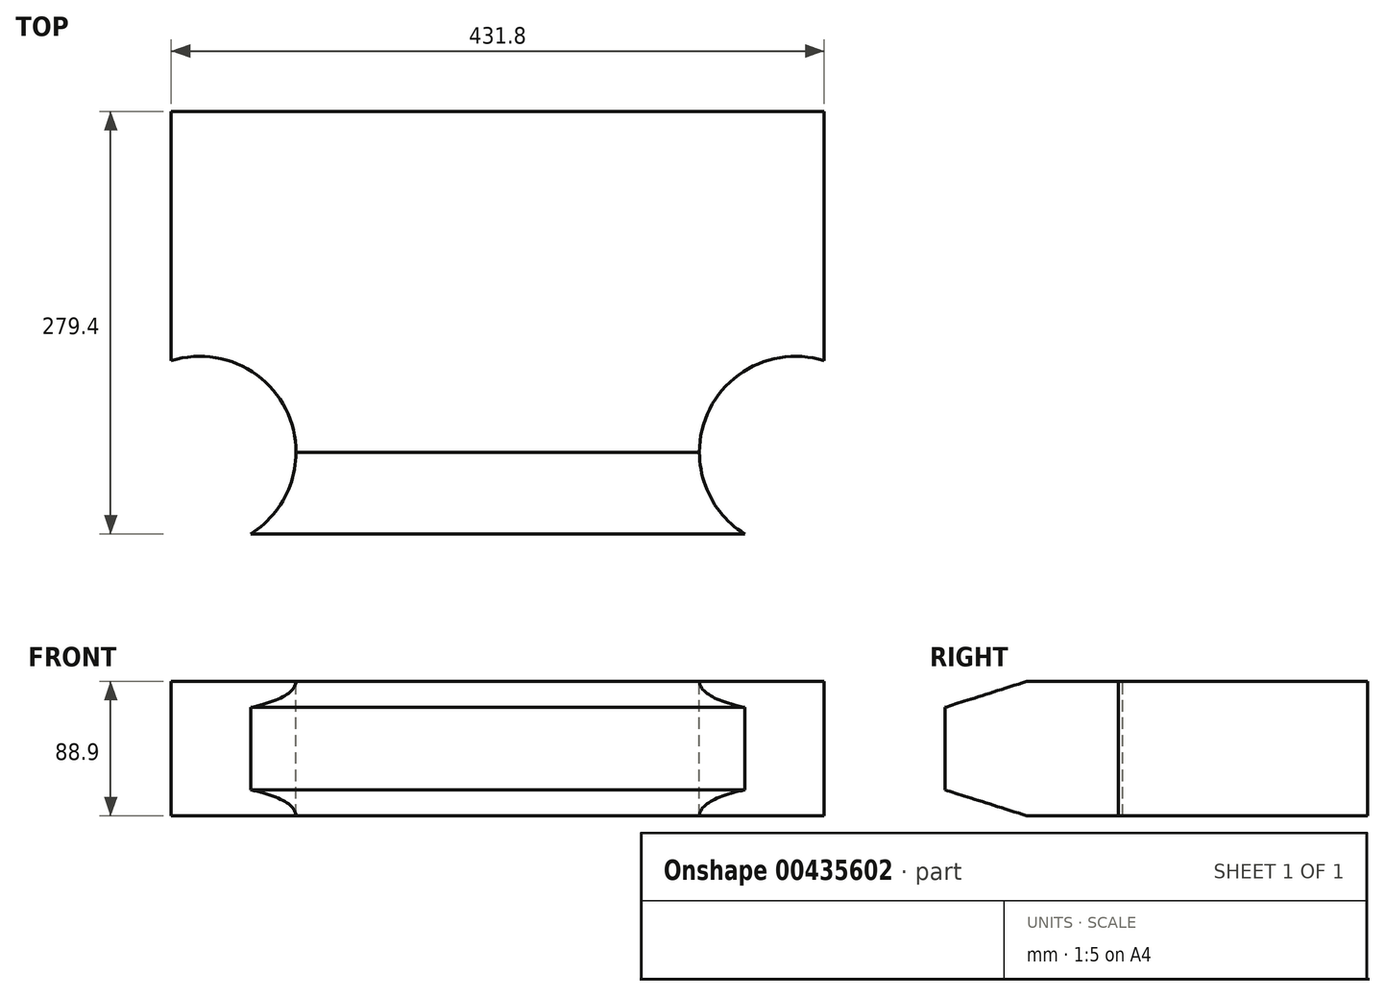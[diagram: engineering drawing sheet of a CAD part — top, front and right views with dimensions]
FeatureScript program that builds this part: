
annotation { "Feature Type Name" : "Feature", "Feature Type Description" : "" }
export const myFeature = defineFeature(function(context is Context, id is Id, definition is map)
    precondition{}
    {
        {
            var Q0;
            Q0=qCreatedBy(makeId("Front.planeOp"),FACE);
            var sketch = newSketch(context, id + "F0", { "sketchPlane" : qUnion([Q0])});
            skLineSegment(sketch, "E0.bottom", {"start": v(-215.9, 44.45) * mm, "end": v(215.9, 44.45) * mm});
            skLineSegment(sketch, "E0.top", {"start": v(-215.9, -44.45) * mm, "end": v(215.9, -44.45) * mm});
            skLineSegment(sketch, "E0.left", {"start": v(-215.9, 44.45) * mm, "end": v(-215.9, -44.45) * mm});
            skLineSegment(sketch, "E0.right", {"start": v(215.9, 44.45) * mm, "end": v(215.9, -44.45) * mm});
            skSolve(sketch);
        }
        {
            var Q0;
            Q0 = qSketchRegion(id + "F0", true);
            extrude(context, id + "F1", {"entities" : qUnion([Q0]), "oppositeDirection" : true, "depth" : 279.4 * mm});
        }
        {
            var Q0;
            Q0=makeQuery(id+"F1.opExtrude","SWEPT_FACE",FACE,{"disambiguationData":[OSD([sQuery(id+"F0.wireOp",EDGE,"E0.bottom")])]});
            var sketch = newSketch(context, id + "F2", { "sketchPlane" : qUnion([Q0])});
            skCircle(sketch, "E1", {"center": v(-196.85, 53.98) * mm, "radius": 63.5 * mm});
            skCircle(sketch, "E2", {"center": v(196.85, 53.98) * mm, "radius": 63.5 * mm});
            skSolve(sketch);
        }
        {
            var Q0;
            Q0 = qSketchRegion(id + "F2", true);
            extrude(context, id + "F3", {"entities" : qUnion([Q0]), "operationType" : NewBodyOperationType.REMOVE, "oppositeDirection" : true, "depth" : 127 * mm});
        }
        {
            var Q0;
            Q0=qCreatedBy(makeId("Right.planeOp"),FACE);
            var sketch = newSketch(context, id + "F4", { "sketchPlane" : qUnion([Q0])});
            skLineSegment(sketch, "E3", {"start": v(0, 27.3) * mm, "end": v(53.98, 44.45) * mm});
            skLineSegment(sketch, "E4", {"start": v(0, 27.3) * mm, "end": v(0, 44.45) * mm});
            skLineSegment(sketch, "E5", {"start": v(0, 44.45) * mm, "end": v(53.98, 44.45) * mm});
            skLineSegment(sketch, "E6", {"start": v(53.98, -44.45) * mm, "end": v(0, -44.45) * mm});
            skLineSegment(sketch, "E7", {"start": v(0, -44.45) * mm, "end": v(0, -27.3) * mm});
            skLineSegment(sketch, "E8", {"start": v(0, -27.3) * mm, "end": v(53.98, -44.45) * mm});
            skSolve(sketch);
        }
        {
            var Q0;
            Q0 = qSketchRegion(id + "F4", true);
            extrude(context, id + "F5", {"entities" : qUnion([Q0]), "operationType" : NewBodyOperationType.REMOVE, "oppositeDirection" : true, "depth" : 227.33 * mm, "hasSecondDirection" : true, "secondDirectionOppositeDirection" : false, "secondDirectionDepth" : 269.24 * mm});
        }
    });
